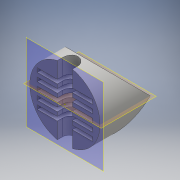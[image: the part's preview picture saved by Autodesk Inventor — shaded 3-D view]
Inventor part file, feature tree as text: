
AUTODESK INVENTOR PART (.ipt)
format: ipt  version: 2016 (Build 200138000, 138)  size: 180,224 bytes
history: native  units: mm
features: sketch x6, extrude x4
ambient origin geometry x8: Origin, YZ Plane, XZ Plane, XY Plane, X Axis, Y Axis, Z Axis, Center Point
bodies: Solid1 (feature_tree)
feature tree (10):
  extrude  "Extrusion1"  Depth=50.0mm TaperAngle=0.0deg
  sketch  "Sketch2"  dims[d3=35.0mm d4=50.0mm d5=50.0mm d6=0.0mm d7=0.0mm]
  extrude  "Extrusion2"  Depth=50.0mm TaperAngle=0.0deg
  extrude  "Extrusion3"  Depth=50.0mm TaperAngle=0.0deg
  sketch  "Sketch5"  dims[d15=30.0mm d17=8.0mm d18=30.0mm d20=8.0mm]
  extrude  "Extrusion4"  Depth=4.0mm
  sketch  "Sketch1"  dims[d0=70.0mm d1=50.0mm d2=0.0mm]
  sketch  "Sketch3"  dims[d8=15.0mm d9=50.0mm d10=50.0mm d11=0.0mm d12=0.0mm]
  sketch  "Sketch4"  dims[d13=55.0mm d14=4.0mm]
  sketch  "Sketch6"  dims[d23=50.0mm d24=0.0mm]
